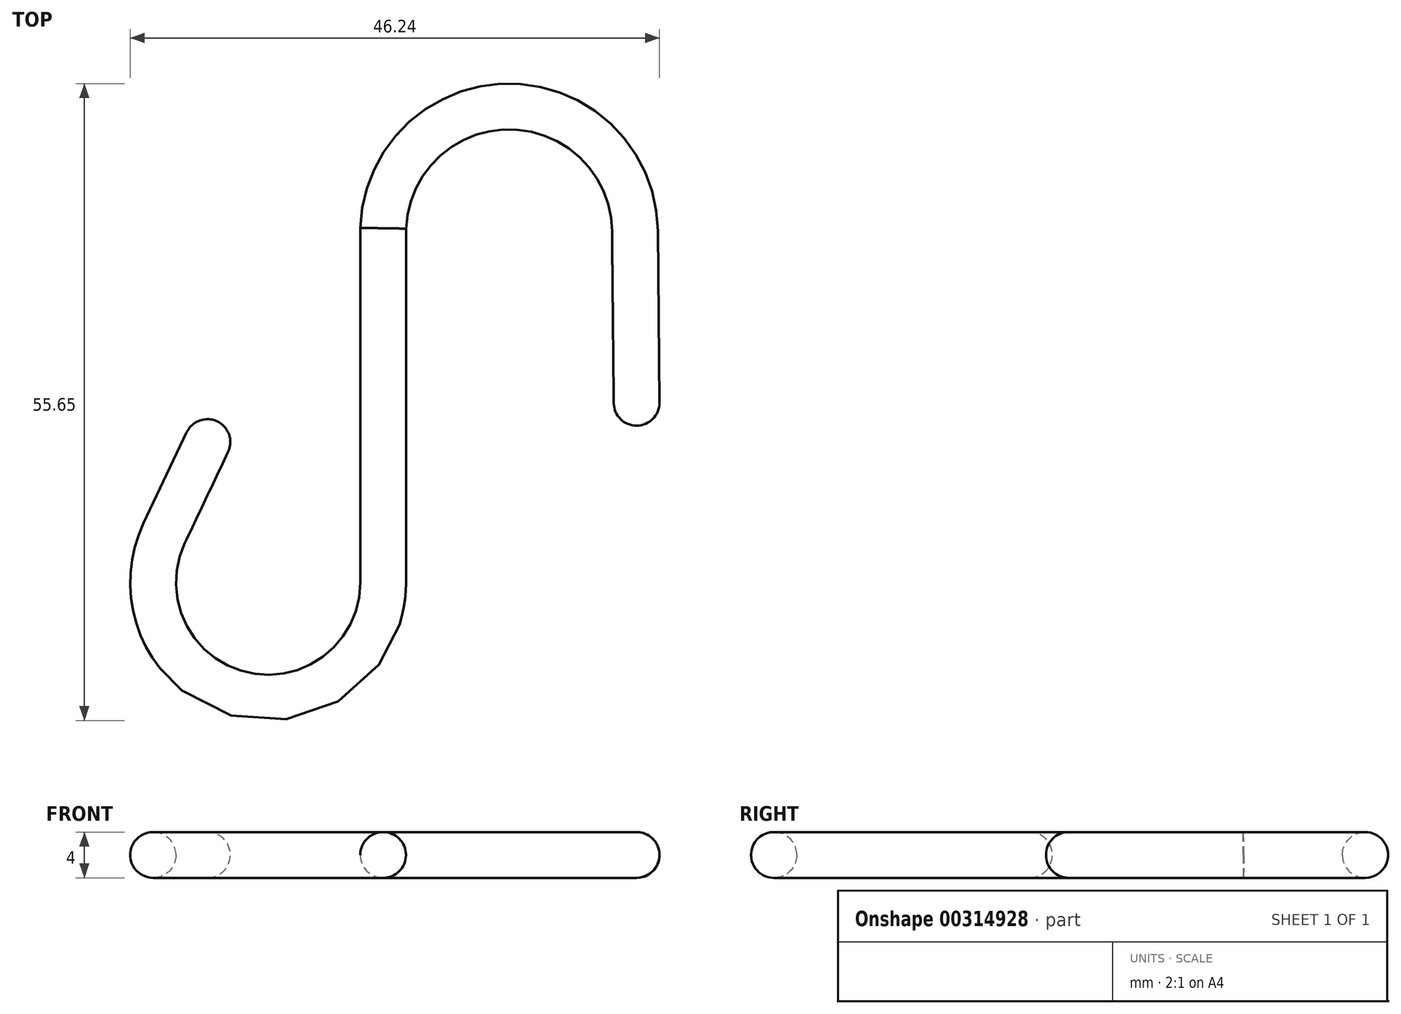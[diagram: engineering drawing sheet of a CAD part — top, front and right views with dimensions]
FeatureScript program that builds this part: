
annotation { "Feature Type Name" : "Feature", "Feature Type Description" : "" }
export const myFeature = defineFeature(function(context is Context, id is Id, definition is map)
    precondition{}
    {
        {
            var Q0;
            Q0=qCreatedBy(makeId("Top.planeOp"),FACE);
            var sketch = newSketch(context, id + "F0", { "sketchPlane" : qUnion([Q0])});
            skArc(sketch, "E0", {"start": v(-3.12, 34.34) * mm, "mid": v(-16, 47.21) * mm, "end": v(-29.12, 34.6) * mm});
            skLineSegment(sketch, "E1", {"start": v(-3.12, 34.34) * mm, "end": v(-2.98, 19.34) * mm});
            skLineSegment(sketch, "E2", {"start": v(-29.12, 34.6) * mm, "end": v(-29.12, 3.6) * mm});
            skArc(sketch, "E3", {"start": v(-44.44, 7.06) * mm, "mid": v(-38.94, -4.25) * mm, "end": v(-29.12, 3.6) * mm});
            skLineSegment(sketch, "E4", {"start": v(-44.44, 7.06) * mm, "end": v(-40.66, 15.03) * mm});
            skLineSegment(sketch, "E5.0", {"start": v(-48.06, 8.77) * mm, "end": v(-44.27, 16.74) * mm});
            skLineSegment(sketch, "E5.1", {"start": v(-7.12, 34.3) * mm, "end": v(-6.98, 19.3) * mm});
            skArc(sketch, "E5.2", {"start": v(-7.12, 34.3) * mm, "mid": v(-16, 43.21) * mm, "end": v(-25.12, 34.54) * mm});
            skLineSegment(sketch, "E5.3", {"start": v(-25.12, 34.54) * mm, "end": v(-25.12, 3.6) * mm});
            skArc(sketch, "E5.4", {"start": v(-48.06, 8.77) * mm, "mid": v(-39.82, -8.15) * mm, "end": v(-25.12, 3.6) * mm});
            skArc(sketch, "E6", {"start": v(-44.27, 16.74) * mm, "mid": v(-41.61, 17.7) * mm, "end": v(-40.66, 15.03) * mm});
            skArc(sketch, "E7", {"start": v(-6.98, 19.3) * mm, "mid": v(-4.96, 17.32) * mm, "end": v(-2.98, 19.34) * mm});
            skSolve(sketch);
        }
        {
            var Q0;
            Q0=makeQuery(id+"F0.imprint","IMPRINT",FACE,{"disambiguationData":[TD([[makeQuery(id+"F0.imprint","IMPRINT",EDGE,{"derivedFrom":sQuery(id+"F0.wireOp",EDGE,"E0")}),1.0]])]});
            extrude(context, id + "F1", {"entities" : qUnion([Q0]), "depth" : 4 * mm});
        }
        {
            var Q0;
            Q0=makeQuery(id+"F1.opExtrude","CAP_FACE",FACE,{"disambiguationData":[OSD([sQuery(id+"F0.wireOp",EDGE,"E0"),sQuery(id+"F0.wireOp",EDGE,"E1"),sQuery(id+"F0.wireOp",EDGE,"E2"),sQuery(id+"F0.wireOp",EDGE,"E3"),sQuery(id+"F0.wireOp",EDGE,"E4"),sQuery(id+"F0.wireOp",EDGE,"E5.0"),sQuery(id+"F0.wireOp",EDGE,"E5.1"),sQuery(id+"F0.wireOp",EDGE,"E5.2"),sQuery(id+"F0.wireOp",EDGE,"E5.3"),sQuery(id+"F0.wireOp",EDGE,"E5.4"),sQuery(id+"F0.wireOp",EDGE,"E6"),sQuery(id+"F0.wireOp",EDGE,"E7")])],"isStart":true});
            var Q1;
            Q1=makeQuery(id+"F1.opExtrude","CAP_FACE",FACE,{"disambiguationData":[OSD([sQuery(id+"F0.wireOp",EDGE,"E0"),sQuery(id+"F0.wireOp",EDGE,"E1"),sQuery(id+"F0.wireOp",EDGE,"E2"),sQuery(id+"F0.wireOp",EDGE,"E3"),sQuery(id+"F0.wireOp",EDGE,"E4"),sQuery(id+"F0.wireOp",EDGE,"E5.0"),sQuery(id+"F0.wireOp",EDGE,"E5.1"),sQuery(id+"F0.wireOp",EDGE,"E5.2"),sQuery(id+"F0.wireOp",EDGE,"E5.3"),sQuery(id+"F0.wireOp",EDGE,"E5.4"),sQuery(id+"F0.wireOp",EDGE,"E6"),sQuery(id+"F0.wireOp",EDGE,"E7")])],"isStart":false});
            fillet(context, id + "F2", {"entities" : qUnion([Q0, Q1]), "radius" : 2 * mm, "tangentPropagation" : true, "allowEdgeOverflow" : false});
        }
    });
